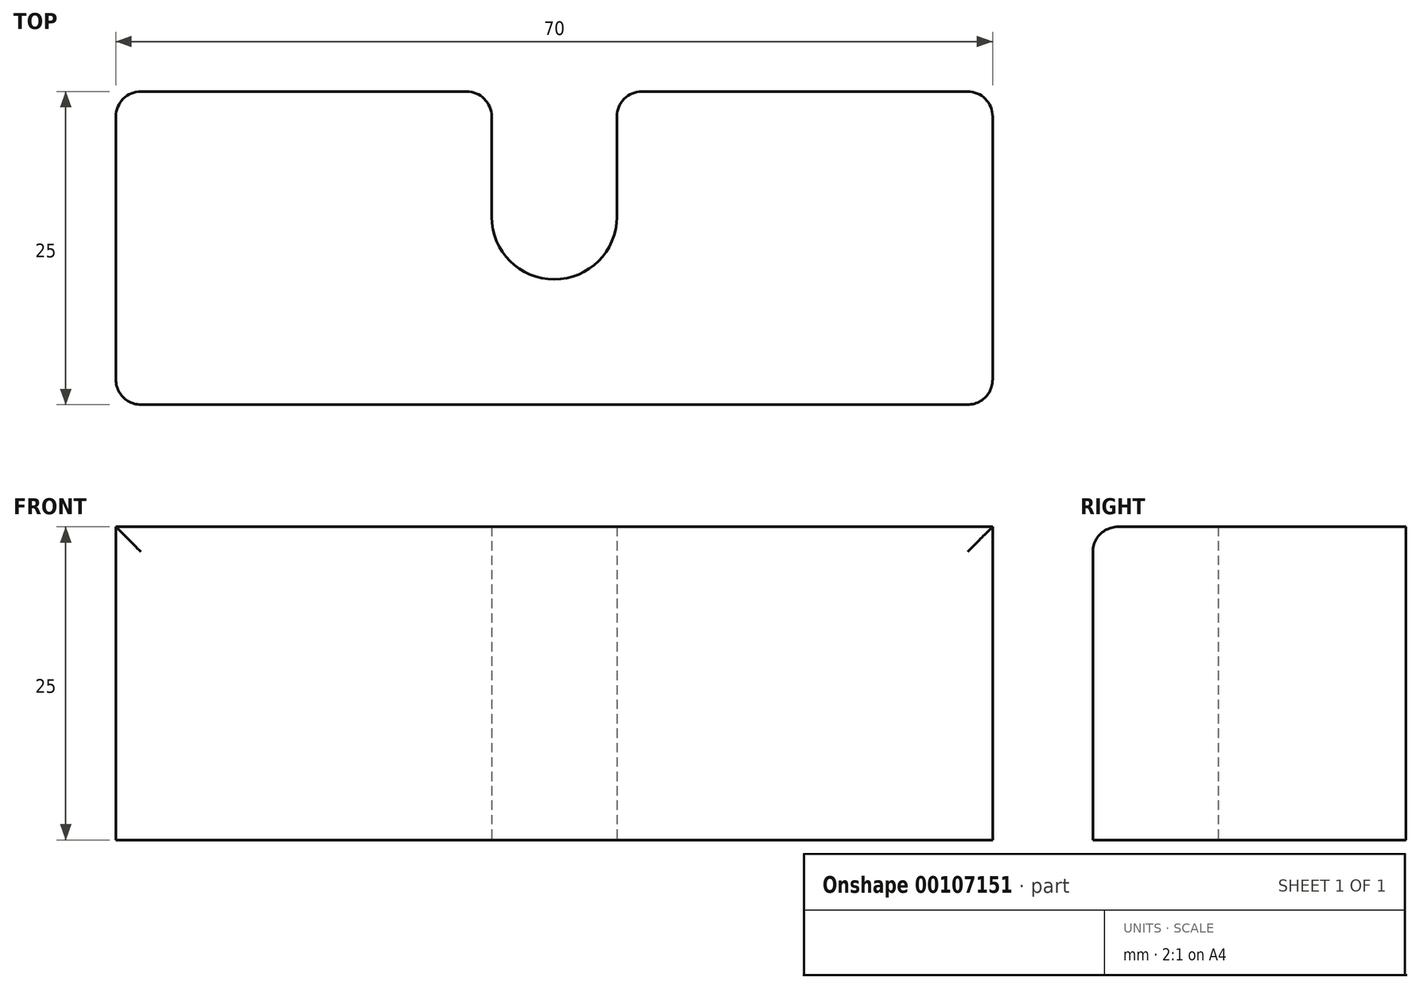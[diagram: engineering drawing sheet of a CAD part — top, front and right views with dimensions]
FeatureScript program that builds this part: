
annotation { "Feature Type Name" : "Feature", "Feature Type Description" : "" }
export const myFeature = defineFeature(function(context is Context, id is Id, definition is map)
    precondition{}
    {
        {
            var Q0;
            Q0=qCreatedBy(makeId("Top.planeOp"),FACE);
            var sketch = newSketch(context, id + "F0", { "sketchPlane" : qUnion([Q0])});
            skLineSegment(sketch, "E0", {"start": v(-34.18, 0) * mm, "end": v(35.82, 0) * mm});
            skLineSegment(sketch, "E1", {"start": v(35.82, 0) * mm, "end": v(35.82, 25) * mm});
            skLineSegment(sketch, "E2", {"start": v(5.82, 25) * mm, "end": v(35.82, 25) * mm});
            skLineSegment(sketch, "E3", {"start": v(5.82, 25) * mm, "end": v(5.82, 15) * mm});
            skLineSegment(sketch, "E4", {"start": v(-34.18, 0) * mm, "end": v(-34.18, 25) * mm});
            skLineSegment(sketch, "E5", {"start": v(-4.18, 25) * mm, "end": v(-34.18, 25) * mm});
            skLineSegment(sketch, "E6", {"start": v(-4.18, 25) * mm, "end": v(-4.18, 15) * mm});
            skArc(sketch, "E7", {"start": v(-4.18, 15) * mm, "mid": v(0.82, 10) * mm, "end": v(5.82, 15) * mm});
            skSolve(sketch);
        }
        {
            var Q0;
            Q0=makeQuery(id+"F0.imprint","IMPRINT",FACE,{"disambiguationData":[TD([[makeQuery(id+"F0.imprint","IMPRINT",EDGE,{"derivedFrom":sQuery(id+"F0.wireOp",EDGE,"E0")}),1.0]])]});
            extrude(context, id + "F1", {"entities" : qUnion([Q0]), "depth" : 25 * mm});
        }
        {
            var Q0;
            Q0=makeQuery(id+"F1.opExtrude","CAP_EDGE",EDGE,{"disambiguationData":[OSD([sQuery(id+"F0.wireOp",EDGE,"E0")])],"isStart":false});
            var Q1;
            Q1=makeQuery(id+"F1.opExtrude","SWEPT_EDGE",EDGE,{"disambiguationData":[OSD([sQuery(id+"F0.wireOp",EDGE,"E0"),sQuery(id+"F0.wireOp",EDGE,"E4")])]});
            var Q2;
            Q2=makeQuery(id+"F1.opExtrude","SWEPT_EDGE",EDGE,{"disambiguationData":[OSD([sQuery(id+"F0.wireOp",EDGE,"E0"),sQuery(id+"F0.wireOp",EDGE,"E1")])]});
            var Q3;
            Q3=makeQuery(id+"F1.opExtrude","SWEPT_EDGE",EDGE,{"disambiguationData":[OSD([sQuery(id+"F0.wireOp",EDGE,"E1"),sQuery(id+"F0.wireOp",EDGE,"E2")])]});
            var Q4;
            Q4=makeQuery(id+"F1.opExtrude","SWEPT_EDGE",EDGE,{"disambiguationData":[OSD([sQuery(id+"F0.wireOp",EDGE,"E2"),sQuery(id+"F0.wireOp",EDGE,"E3")])]});
            var Q5;
            Q5=makeQuery(id+"F1.opExtrude","SWEPT_EDGE",EDGE,{"disambiguationData":[OSD([sQuery(id+"F0.wireOp",EDGE,"E5"),sQuery(id+"F0.wireOp",EDGE,"E6")])]});
            var Q6;
            Q6=makeQuery(id+"F1.opExtrude","SWEPT_EDGE",EDGE,{"disambiguationData":[OSD([sQuery(id+"F0.wireOp",EDGE,"E4"),sQuery(id+"F0.wireOp",EDGE,"E5")])]});
            fillet(context, id + "F2", {"entities" : qUnion([Q0, Q1, Q2, Q3, Q4, Q5, Q6]), "radius" : 2 * mm, "tangentPropagation" : true, "allowEdgeOverflow" : false});
        }
    });
